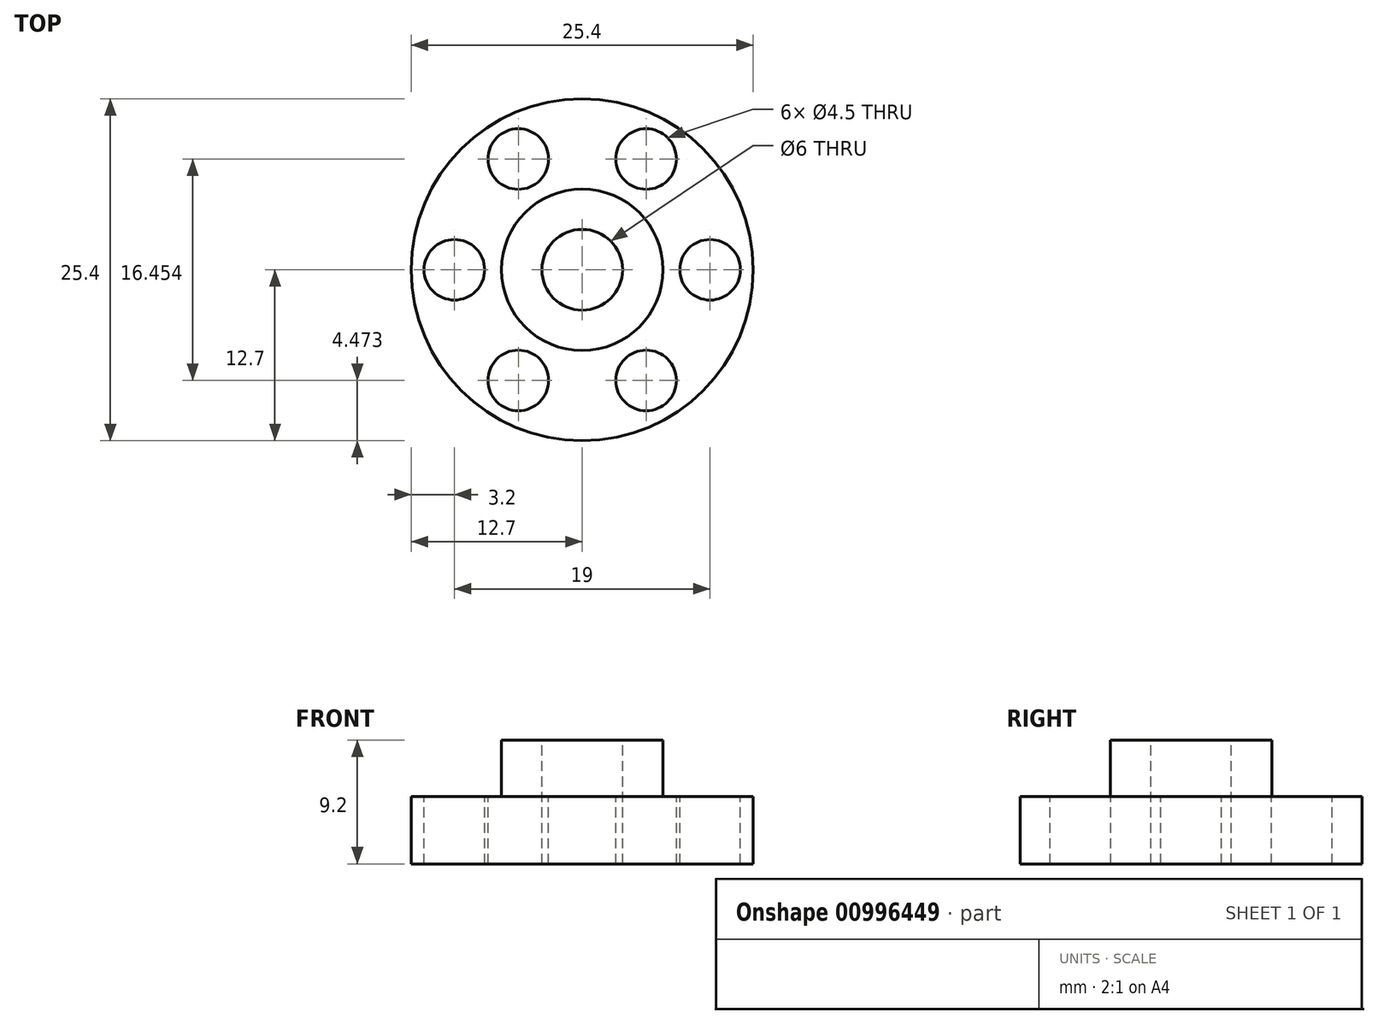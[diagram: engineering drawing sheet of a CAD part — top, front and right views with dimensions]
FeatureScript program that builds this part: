
annotation { "Feature Type Name" : "Feature", "Feature Type Description" : "" }
export const myFeature = defineFeature(function(context is Context, id is Id, definition is map)
    precondition{}
    {
        {
            var Q0;
            Q0=qCreatedBy(makeId("Front.planeOp"),FACE);
            var sketch = newSketch(context, id + "F0", { "sketchPlane" : qUnion([Q0])});
            skLineSegment(sketch, "E0", {"start": v(0, 0) * mm, "end": v(-12.7, 0) * mm});
            skLineSegment(sketch, "E1", {"start": v(-12.7, 0) * mm, "end": v(-12.7, 5) * mm});
            skLineSegment(sketch, "E2", {"start": v(-12.7, 5) * mm, "end": v(-6, 5) * mm});
            skLineSegment(sketch, "E3", {"start": v(-6, 5) * mm, "end": v(-6, 9.2) * mm});
            skLineSegment(sketch, "E4", {"start": v(-6, 9.2) * mm, "end": v(0, 9.2) * mm});
            skLineSegment(sketch, "E5", {"start": v(0, 9.2) * mm, "end": v(0, 0) * mm});
            skLineSegment(sketch, "E6", {"start": v(-3, 9.2) * mm, "end": v(-3, 0) * mm});
            skSolve(sketch);
        }
        {
            var Q0;
            {var subQ1=sQuery(id+"F0.wireOp",EDGE,"E1");Q0=makeQuery(id+"F0.imprint","IMPRINT",FACE,{"disambiguationData":[TD([[makeQuery(id+"F0.imprint","IMPRINT",EDGE,{"derivedFrom":subQ1}),-1.0]])]});}
            var Q1;
            Q1=sQuery(id+"F0.wireOp",EDGE,"E5");
            revolve(context, id + "F1", {"surfaceOperationType" : NewSurfaceOperationType.NEW, "entities" : qUnion([Q0]), "axis" : qUnion([Q1]), "revolveType" : RevolveType.FULL});
        }
        {
            var Q0;
            Q0=makeQuery(id+"F1.opRevolve","SWEPT_FACE",FACE,{"disambiguationData":[OSD([sQuery(id+"F0.wireOp",EDGE,"E2")])]});
            var sketch = newSketch(context, id + "F2", { "sketchPlane" : qUnion([Q0])});
            skCircle(sketch, "E7", {"center": v(0, 0) * mm, "radius": 9.5 * mm, "construction": true});
            skLineSegment(sketch, "E8.0", {"start": v(-4.75, 8.23) * mm, "end": v(4.75, 8.23) * mm, "construction": true});
            skLineSegment(sketch, "E8.1", {"start": v(4.75, 8.23) * mm, "end": v(9.5, 0) * mm, "construction": true});
            skLineSegment(sketch, "E8.2", {"start": v(9.5, 0) * mm, "end": v(4.75, -8.23) * mm, "construction": true});
            skLineSegment(sketch, "E8.3", {"start": v(4.75, -8.23) * mm, "end": v(-4.75, -8.23) * mm, "construction": true});
            skLineSegment(sketch, "E8.4", {"start": v(-4.75, -8.23) * mm, "end": v(-9.5, 0) * mm, "construction": true});
            skLineSegment(sketch, "E8.5", {"start": v(-9.5, 0) * mm, "end": v(-4.75, 8.23) * mm, "construction": true});
            skLineSegment(sketch, "E9", {"start": v(-9.5, 0) * mm, "end": v(9.5, 0) * mm, "construction": true});
            skPoint(sketch, "E10", {"position": v(-4.75, 8.23) * mm});
            skPoint(sketch, "E11", {"position": v(-9.5, 0) * mm});
            skSolve(sketch);
        }
        {
            var Q0;
            Q0=sQuery(id+"F2.wireOp",VERTEX,"E10");
            var Q1;
            Q1=sQuery(id+"F2.wireOp",VERTEX,"E11");
            var Q2;
            Q2=sQuery(id+"F2.wireOp",VERTEX,"E8.3.end");
            var Q3;
            Q3=sQuery(id+"F2.wireOp",VERTEX,"E8.2.end");
            var Q4;
            Q4=sQuery(id+"F2.wireOp",VERTEX,"E8.1.end");
            var Q5;
            Q5=sQuery(id+"F2.wireOp",VERTEX,"E8.0.end");
            var Q6;
            Q6=makeQuery(id+"F1.opRevolve","SWEPT_BODY",BODY,{"disambiguationData":[OSD([sQuery(id+"F0.wireOp",EDGE,"E0"),sQuery(id+"F0.wireOp",EDGE,"E1"),sQuery(id+"F0.wireOp",EDGE,"E2"),sQuery(id+"F0.wireOp",EDGE,"E3"),sQuery(id+"F0.wireOp",EDGE,"E4"),sQuery(id+"F0.wireOp",EDGE,"E6")])]});
            hole(context, id + "F3", {"style" : HoleStyle.SIMPLE, "endStyle" : HoleEndStyle.BLIND, "standardTappedOrClearance" : lookupTablePath({ "fit" : "Normal", "standard" : "ISO", "size" : "M4", "type" : "Clearance" }), "standardBlindInLast" : lookupTablePath({ "fit" : "Normal", "standard" : "ISO", "engagement" : "75%", "pitch" : "0.7 mm", "size" : "M4", "type" : "Clearance & tapped" }), "holeDiameter" : 4.5 * mm, "majorDiameter" : 5 * mm, "holeDepth" : 7 * mm, "isTappedThrough" : true, "tappedDepth" : 5.5 * mm, "tapClearance" : 3, "locations" : qUnion([Q0, Q1, Q2, Q3, Q4, Q5]), "scope" : qUnion([Q6])});
        }
    });
